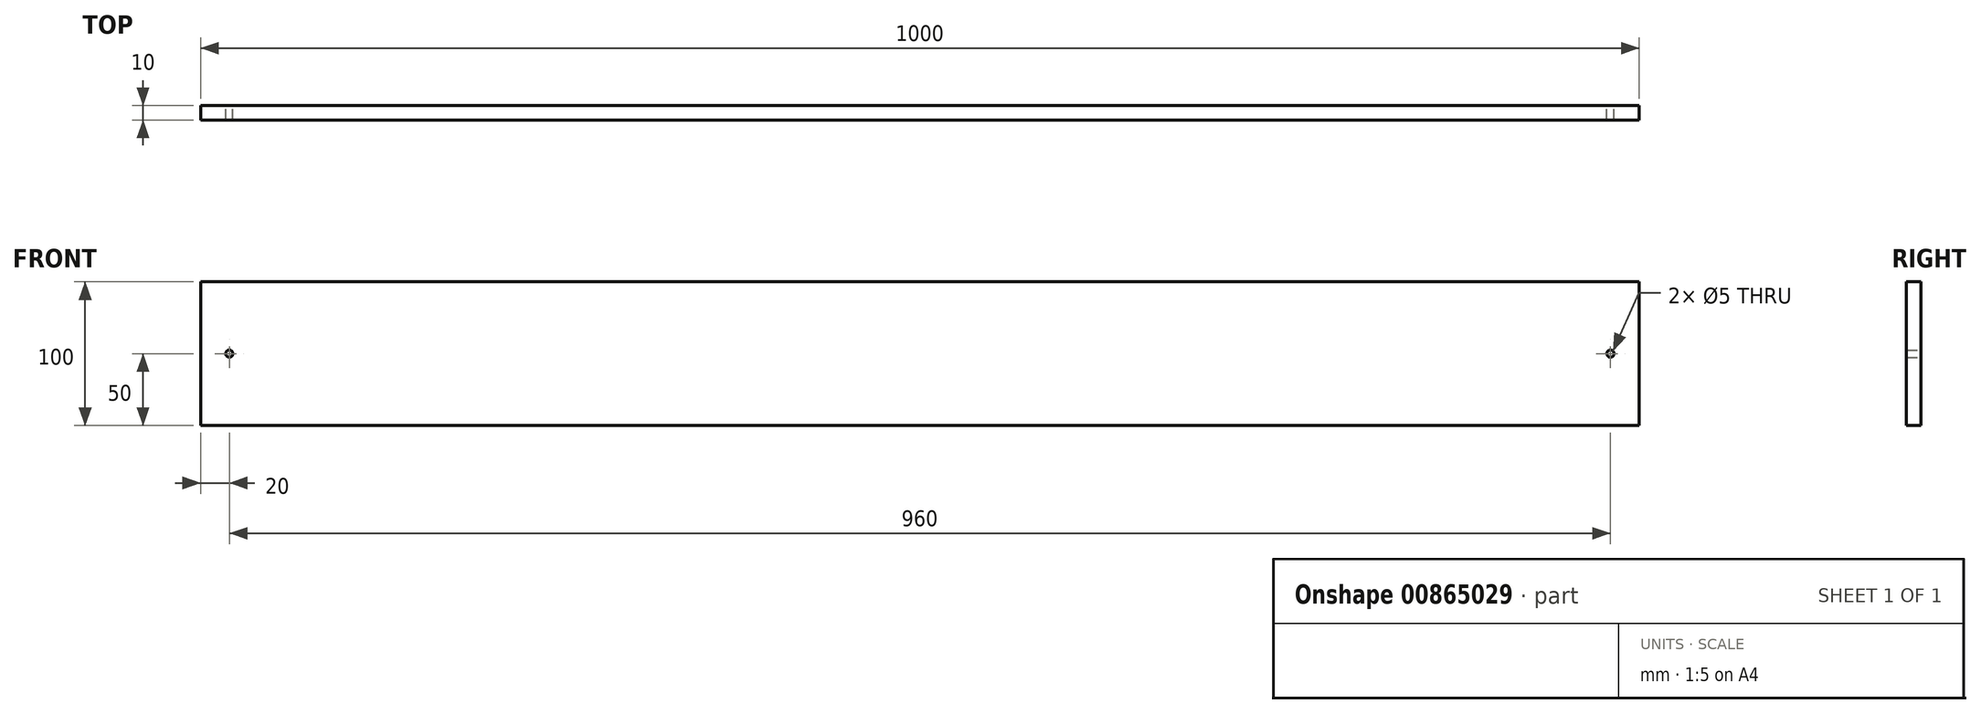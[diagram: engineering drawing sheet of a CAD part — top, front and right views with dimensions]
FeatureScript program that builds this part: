
annotation { "Feature Type Name" : "Feature", "Feature Type Description" : "" }
export const myFeature = defineFeature(function(context is Context, id is Id, definition is map)
    precondition{}
    {
        {
            var Q0;
            Q0=qCreatedBy(makeId("Front.planeOp"),FACE);
            var sketch = newSketch(context, id + "F0", { "sketchPlane" : qUnion([Q0])});
            skLineSegment(sketch, "E0.bottom", {"start": v(500, 50) * mm, "end": v(-500, 50) * mm});
            skLineSegment(sketch, "E0.top", {"start": v(500, -50) * mm, "end": v(-500, -50) * mm});
            skLineSegment(sketch, "E0.left", {"start": v(500, 50) * mm, "end": v(500, -50) * mm});
            skLineSegment(sketch, "E0.right", {"start": v(-500, 50) * mm, "end": v(-500, -50) * mm});
            skPoint(sketch, "E0.middle", {"position": v(0, 0) * mm});
            skLineSegment(sketch, "E1", {"start": v(-460, 50) * mm, "end": v(-460, -50) * mm, "construction": true});
            skLineSegment(sketch, "E2", {"start": v(-460, 0) * mm, "end": v(-500, 0) * mm, "construction": true});
            skLineSegment(sketch, "E3", {"start": v(460, 50) * mm, "end": v(460, -50) * mm, "construction": true});
            skLineSegment(sketch, "E4", {"start": v(460, 0) * mm, "end": v(500, 0) * mm, "construction": true});
            skPoint(sketch, "E5", {"position": v(-480, 0) * mm});
            skPoint(sketch, "E6", {"position": v(480, 0) * mm});
            skSolve(sketch);
        }
        {
            var Q0;
            Q0 = qSketchRegion(id + "F0", true);
            extrude(context, id + "F1", {"entities" : qUnion([Q0]), "depth" : 10 * mm, "offsetDistance" : 25 * mm});
        }
        {
            var Q0;
            Q0=sQuery(id+"F0.wireOp",VERTEX,"E5");
            var Q1;
            Q1=sQuery(id+"F0.wireOp",VERTEX,"E6");
            var Q2;
            Q2=makeQuery(id+"F1.opExtrude","SWEPT_BODY",BODY,{"disambiguationData":[OSD([sQuery(id+"F0.wireOp",EDGE,"E0.bottom"),sQuery(id+"F0.wireOp",EDGE,"E0.top"),sQuery(id+"F0.wireOp",EDGE,"E0.left"),sQuery(id+"F0.wireOp",EDGE,"E0.right")])]});
            hole(context, id + "F2", {"style" : HoleStyle.SIMPLE, "endStyle" : HoleEndStyle.THROUGH, "oppositeDirection" : true, "holeDiameter" : 5 * mm, "majorDiameter" : 5 * mm, "isTappedThrough" : true, "tappedDepth" : 12 * mm, "tapClearance" : 3, "locations" : qUnion([Q0, Q1]), "scope" : qUnion([Q2])});
        }
    });
